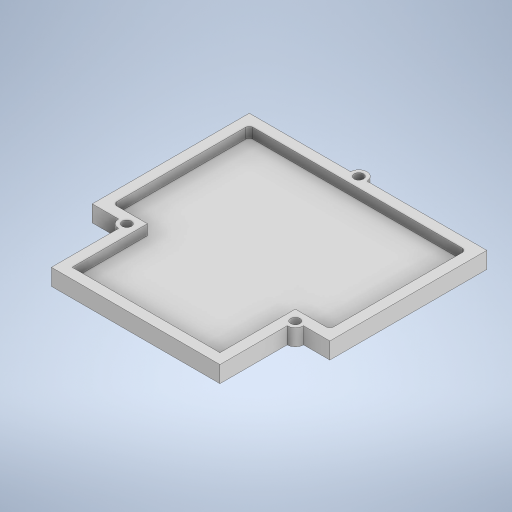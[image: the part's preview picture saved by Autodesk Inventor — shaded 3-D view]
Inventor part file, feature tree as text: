
AUTODESK INVENTOR PART (.ipt)
format: ipt  version: 2024 (Build 280153000, 153)  size: 304,128 bytes
history: native  units: in
note: dims shown in document units (in); Inventor stores cm internally (conversion verified against a paired STEP export)
features: extrude x2, sketch x2
ambient origin geometry x8: Origin, YZ Plane, XZ Plane, XY Plane, X Axis, Y Axis, Z Axis, Center Point
bodies: Solid1 (feature_tree)
feature tree (4):
  extrude  "Extrusion1"  Depth=0.1969in
  extrude  "Extrusion2"  Depth=0.1181in
  sketch  "Sketch1"  dims[d0=0.1969in d2=0.1969in]
  sketch  "Sketch2"  dims[d3=0.1969in d4=0.1772in d5=0.1772in d6=0.1772in d7=0.315in d8=0.315in d9=0.315in d10=0.1969in d11=0.0in d12=0.1181in d13=0.0in]
